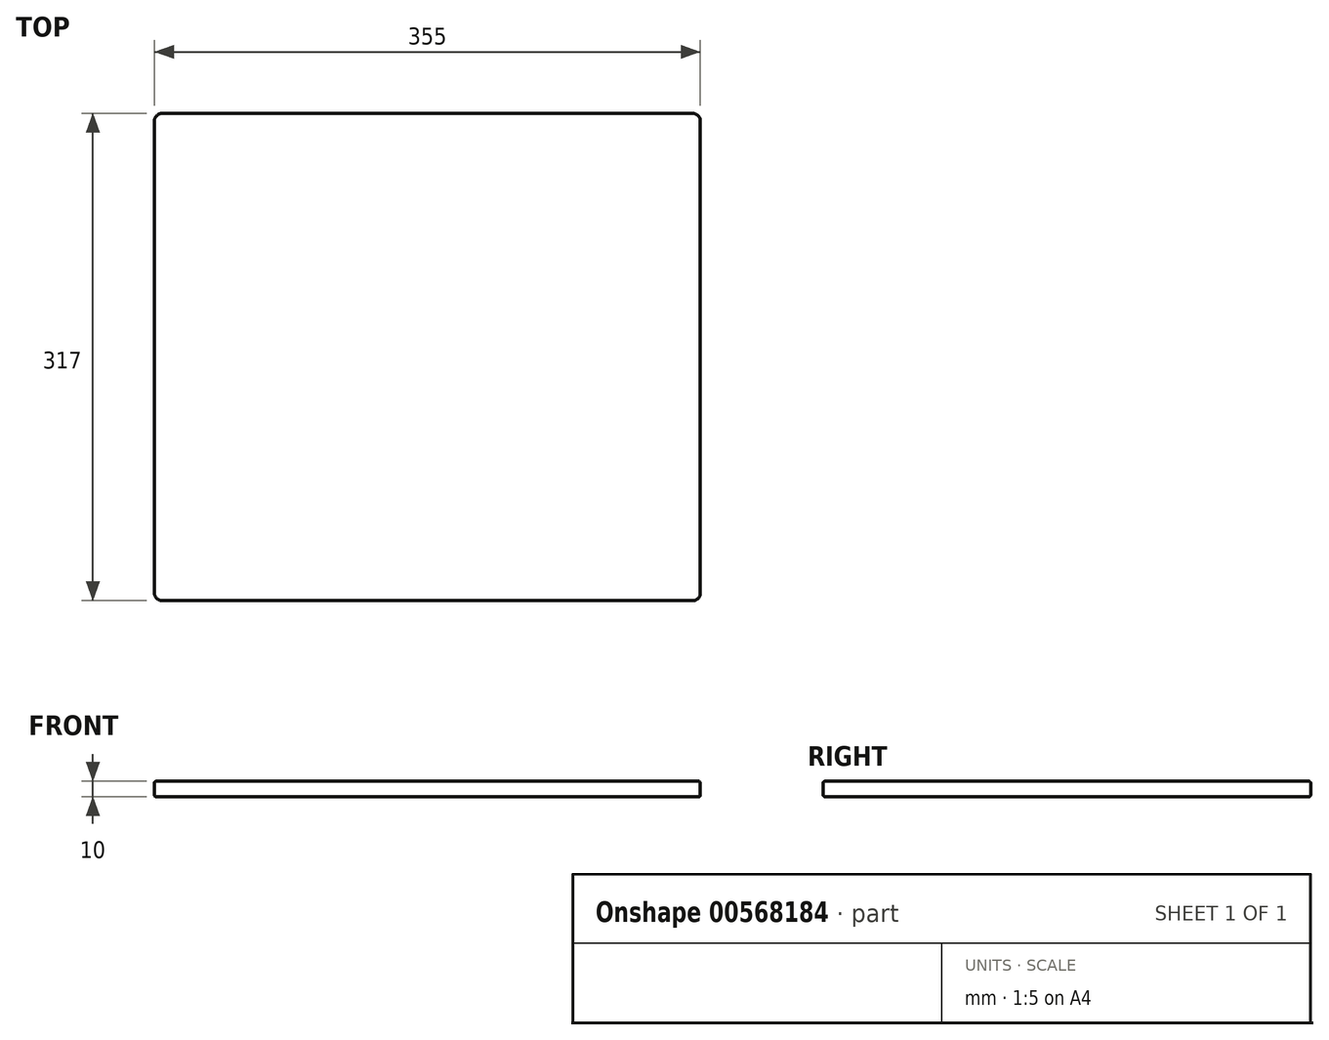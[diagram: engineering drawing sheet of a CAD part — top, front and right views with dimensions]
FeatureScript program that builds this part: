
annotation { "Feature Type Name" : "Feature", "Feature Type Description" : "" }
export const myFeature = defineFeature(function(context is Context, id is Id, definition is map)
    precondition{}
    {
        {
            var Q0;
            Q0=qCreatedBy(makeId("Top.planeOp"),FACE);
            var sketch = newSketch(context, id + "F0", { "sketchPlane" : qUnion([Q0])});
            skLineSegment(sketch, "E0.bottom", {"start": v(5, 0) * mm, "end": v(350, 0) * mm});
            skLineSegment(sketch, "E0.top", {"start": v(5, 317) * mm, "end": v(350, 317) * mm});
            skLineSegment(sketch, "E0.left", {"start": v(0, 5) * mm, "end": v(0, 312) * mm});
            skLineSegment(sketch, "E0.right", {"start": v(355, 5) * mm, "end": v(355, 312) * mm});
            skPoint(sketch, "E1.visualSharp", {"position": v(0, 317) * mm});
            skArc(sketch, "E1.filletArc", {"start": v(5, 317) * mm, "mid": v(1.46, 315.54) * mm, "end": v(0, 312) * mm});
            skPoint(sketch, "E2.visualSharp", {"position": v(355, 317) * mm});
            skArc(sketch, "E2.filletArc", {"start": v(355, 312) * mm, "mid": v(353.54, 315.54) * mm, "end": v(350, 317) * mm});
            skPoint(sketch, "E3.visualSharp", {"position": v(355, 0) * mm});
            skArc(sketch, "E3.filletArc", {"start": v(350, 0) * mm, "mid": v(353.54, 1.46) * mm, "end": v(355, 5) * mm});
            skPoint(sketch, "E4.visualSharp", {"position": v(0, 0) * mm});
            skArc(sketch, "E4.filletArc", {"start": v(0, 5) * mm, "mid": v(1.46, 1.46) * mm, "end": v(5, 0) * mm});
            skSolve(sketch);
        }
        {
            var Q0;
            Q0 = qSketchRegion(id + "F0", true);
            extrude(context, id + "F1", {"entities" : qUnion([Q0]), "depth" : 10 * mm, "offsetDistance" : 25 * mm});
        }
        {
            var Q0;
            Q0=makeQuery(id+"F1.opExtrude","CAP_FACE",FACE,{"disambiguationData":[OSD([sQuery(id+"F0.wireOp",EDGE,"E0.bottom"),sQuery(id+"F0.wireOp",EDGE,"E0.top"),sQuery(id+"F0.wireOp",EDGE,"E0.left"),sQuery(id+"F0.wireOp",EDGE,"E0.right"),sQuery(id+"F0.wireOp",EDGE,"E1.filletArc"),sQuery(id+"F0.wireOp",EDGE,"E2.filletArc"),sQuery(id+"F0.wireOp",EDGE,"E3.filletArc"),sQuery(id+"F0.wireOp",EDGE,"E4.filletArc")])],"isStart":false});
            var Q1;
            Q1=makeQuery(id+"F1.opExtrude","CAP_FACE",FACE,{"disambiguationData":[OSD([sQuery(id+"F0.wireOp",EDGE,"E0.bottom"),sQuery(id+"F0.wireOp",EDGE,"E0.top"),sQuery(id+"F0.wireOp",EDGE,"E0.left"),sQuery(id+"F0.wireOp",EDGE,"E0.right"),sQuery(id+"F0.wireOp",EDGE,"E1.filletArc"),sQuery(id+"F0.wireOp",EDGE,"E2.filletArc"),sQuery(id+"F0.wireOp",EDGE,"E3.filletArc"),sQuery(id+"F0.wireOp",EDGE,"E4.filletArc")])],"isStart":true});
            fillet(context, id + "F2", {"entities" : qUnion([Q0, Q1]), "radius" : 1 * mm, "tangentPropagation" : true, "allowEdgeOverflow" : false});
        }
    });
